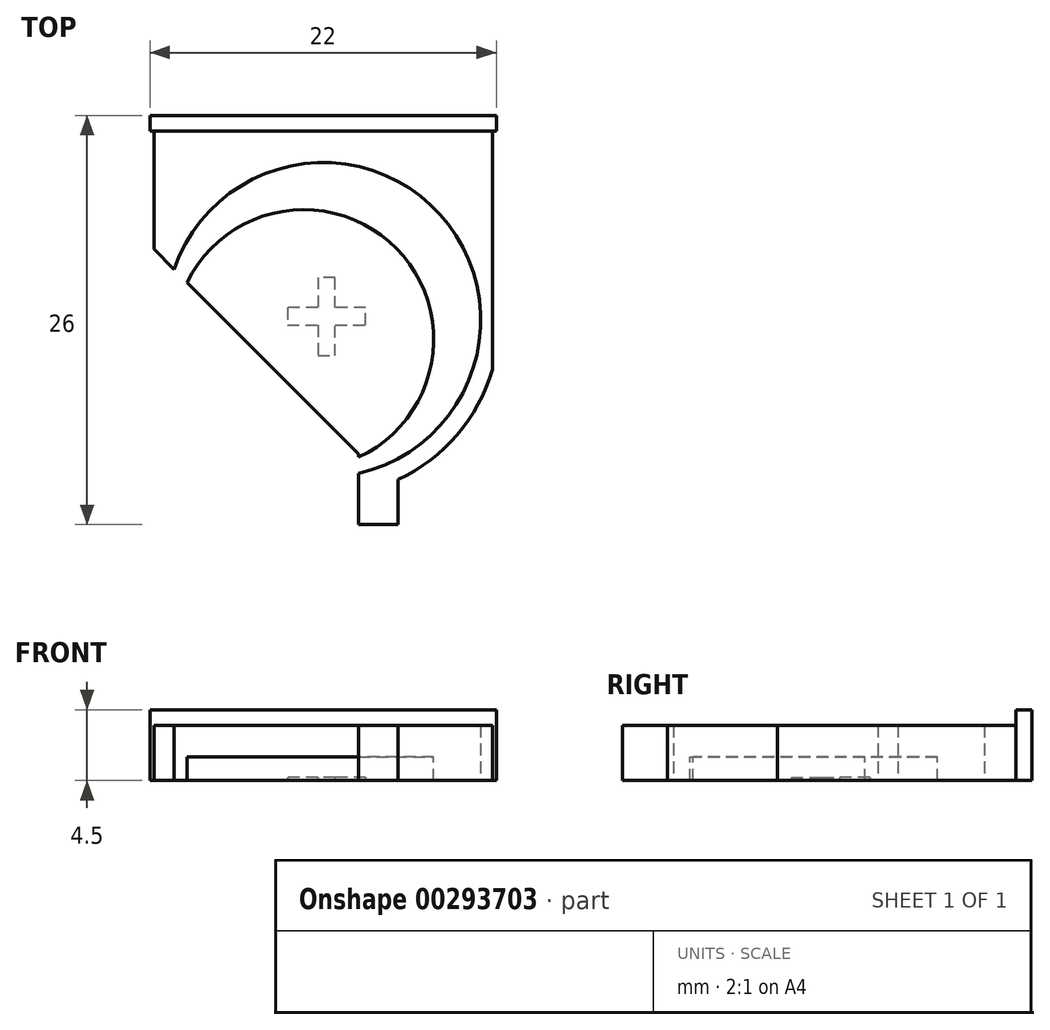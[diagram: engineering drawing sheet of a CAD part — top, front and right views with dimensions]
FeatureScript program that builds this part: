
annotation { "Feature Type Name" : "Feature", "Feature Type Description" : "" }
export const myFeature = defineFeature(function(context is Context, id is Id, definition is map)
    precondition{}
    {
        {
            var Q0;
            Q0=qCreatedBy(makeId("Top.planeOp"),FACE);
            var sketch = newSketch(context, id + "F0", { "sketchPlane" : qUnion([Q0])});
            skLineSegment(sketch, "E0", {"start": v(0, 13) * mm, "end": v(-11, 13) * mm});
            skLineSegment(sketch, "E1", {"start": v(0, 13) * mm, "end": v(11, 13) * mm});
            skLineSegment(sketch, "E2", {"start": v(11, 13) * mm, "end": v(11, 12) * mm});
            skLineSegment(sketch, "E3", {"start": v(-11, 13) * mm, "end": v(-11, 12) * mm});
            skLineSegment(sketch, "E4", {"start": v(-11, 12) * mm, "end": v(11, 12) * mm});
            skPoint(sketch, "E5", {"position": v(-10.75, 12) * mm});
            skPoint(sketch, "E6", {"position": v(10.75, 12) * mm});
            skPoint(sketch, "E7", {"position": v(0, 12) * mm});
            skLineSegment(sketch, "E8", {"start": v(-10.75, 12) * mm, "end": v(-10.75, 9.5) * mm});
            skLineSegment(sketch, "E9", {"start": v(10.75, 12) * mm, "end": v(10.75, 9.5) * mm});
            skLineSegment(sketch, "E10", {"start": v(-10.75, 9.5) * mm, "end": v(10.75, 9.5) * mm});
            skLineSegment(sketch, "E11", {"start": v(-10.75, 9.5) * mm, "end": v(-10.75, 4.5) * mm});
            skLineSegment(sketch, "E12", {"start": v(10.75, 9.5) * mm, "end": v(10.75, -3.14) * mm});
            skArc(sketch, "E13", {"start": v(10.75, -3.14) * mm, "mid": v(8.5, -7.29) * mm, "end": v(4.75, -10.14) * mm});
            skLineSegment(sketch, "E14", {"start": v(4.75, -10.14) * mm, "end": v(4.75, -13) * mm});
            skLineSegment(sketch, "E15", {"start": v(4.75, -13) * mm, "end": v(2.25, -13) * mm});
            skLineSegment(sketch, "E16", {"start": v(2.25, -13) * mm, "end": v(2.25, -8.5) * mm});
            skLineSegment(sketch, "E17", {"start": v(-10.75, 4.5) * mm, "end": v(2.25, -8.5) * mm});
            skLineSegment(sketch, "E18", {"start": v(-10.75, 4.5) * mm, "end": v(10.75, 4.5) * mm, "construction": true});
            skArc(sketch, "E19", {"start": v(-9.47, 3.22) * mm, "mid": v(7.42, 6.7) * mm, "end": v(2.25, -9.74) * mm});
            skCircle(sketch, "E20", {"center": v(-1.24, -1.24) * mm, "radius": 8.25 * mm});
            skArc(sketch, "E21", {"start": v(-9.47, 3.22) * mm, "mid": v(-7.42, -6.7) * mm, "end": v(2.25, -9.74) * mm, "construction": true});
            skLineSegment(sketch, "E22", {"start": v(4.6, 4.6) * mm, "end": v(-7.07, -7.07) * mm});
            skSolve(sketch);
        }
        {
            var Q0;
            Q0=makeQuery(id+"F0.imprint","IMPRINT",FACE,{"disambiguationData":[TD([[makeQuery(id+"F0.imprint","IMPRINT",EDGE,{"derivedFrom":sQuery(id+"F0.wireOp",EDGE,"E0")}),1.0]])]});
            extrude(context, id + "F1", {"entities" : qUnion([Q0]), "depth" : 2.5 * mm, "hasSecondDirection" : true, "secondDirectionOppositeDirection" : true, "secondDirectionDepth" : 2 * mm});
        }
        {
            var Q0;
            {var subQ1=sQuery(id+"F0.wireOp",EDGE,"E8");Q0=makeQuery(id+"F0.imprint","IMPRINT",FACE,{"disambiguationData":[TD([[makeQuery(id+"F0.imprint","IMPRINT",EDGE,{"derivedFrom":subQ1}),1.0]])]});}
            var Q1;
            {var subQ0=sQuery(id+"F0.wireOp",EDGE,"E12");Q1=makeQuery(id+"F0.imprint","IMPRINT",FACE,{"disambiguationData":[TD([[makeQuery(id+"F0.imprint","IMPRINT",EDGE,{"derivedFrom":subQ0}),-1.0]])]});}
            var Q2;
            {var subQ0=sQuery(id+"F0.wireOp",EDGE,"E11");Q2=makeQuery(id+"F0.imprint","IMPRINT",FACE,{"disambiguationData":[TD([[makeQuery(id+"F0.imprint","IMPRINT",EDGE,{"derivedFrom":subQ0}),1.0]])]});}
            var Q3;
            {var subQ0=sQuery(id+"F0.wireOp",EDGE,"E19");var subQ3=sQuery(id+"F0.wireOp",EDGE,"E10");var subQ4=makeQuery(id+"F0.imprint","INTERSECT",VERTEX,{"disambiguationData":[OD(0.0)],"derivedFrom":[subQ3,subQ0]});Q3=makeQuery(id+"F0.imprint","IMPRINT",FACE,{"disambiguationData":[TD([[makeQuery(id+"F0.imprint","IMPRINT",EDGE,{"disambiguationData":[TD([[subQ4,-1.0]])],"derivedFrom":subQ3}),-1.0]])]});}
            var Q4;
            {var subQ0=sQuery(id+"F0.wireOp",EDGE,"E19");var subQ1=sQuery(id+"F0.wireOp",EDGE,"E10");var subQ2=makeQuery(id+"F0.imprint","INTERSECT",VERTEX,{"disambiguationData":[OD(0.0)],"derivedFrom":[subQ1,subQ0]});Q4=makeQuery(id+"F0.imprint","IMPRINT",FACE,{"disambiguationData":[TD([[makeQuery(id+"F0.imprint","IMPRINT",EDGE,{"disambiguationData":[TD([[subQ2,-1.0]])],"derivedFrom":subQ1}),1.0]])]});}
            extrude(context, id + "F2", {"entities" : qUnion([Q0, Q1, Q2, Q3, Q4]), "operationType" : NewBodyOperationType.ADD, "depth" : 1.5 * mm, "hasSecondDirection" : true, "secondDirectionOppositeDirection" : true, "secondDirectionDepth" : 2 * mm});
        }
        {
            var Q0;
            {var subQ0=sQuery(id+"F0.wireOp",EDGE,"E20");var subQ1=sQuery(id+"F0.wireOp",EDGE,"E17");var subQ2=makeQuery(id+"F0.imprint","INTERSECT",VERTEX,{"derivedFrom":[subQ1,subQ0]});Q0=makeQuery(id+"F0.imprint","IMPRINT",FACE,{"disambiguationData":[TD([[makeQuery(id+"F0.imprint","IMPRINT",EDGE,{"disambiguationData":[TD([[subQ2,-1.0]])],"derivedFrom":subQ1}),1.0]])]});}
            var Q1;
            {var subQ0=sQuery(id+"F0.wireOp",EDGE,"E17");var subQ1=sQuery(id+"F0.wireOp",EDGE,"E16");var subQ2=makeQuery(id+"F0.imprint","INTERSECT",VERTEX,{"derivedFrom":[subQ1,subQ0]});Q1=makeQuery(id+"F0.imprint","IMPRINT",FACE,{"disambiguationData":[TD([[makeQuery(id+"F0.imprint","IMPRINT",EDGE,{"disambiguationData":[TD([[subQ2,1.0]])],"derivedFrom":subQ1}),-1.0]])]});}
            var Q2;
            Q2=sQuery(id+"F0.wireOp",EDGE,"E20");
            extrude(context, id + "F3", {"entities" : qUnion([Q0, Q1]), "operationType" : NewBodyOperationType.ADD, "surfaceEntities" : qUnion([Q2]), "oppositeDirection" : true, "depth" : 2 * mm});
        }
        {
            var Q0;
            {var subQ0=sQuery(id+"F0.wireOp",EDGE,"E20");var subQ1=sQuery(id+"F0.wireOp",EDGE,"E17");var subQ2=makeQuery(id+"F0.imprint","INTERSECT",VERTEX,{"derivedFrom":[subQ1,subQ0]});Q0=makeQuery(id+"F0.imprint","IMPRINT",FACE,{"disambiguationData":[TD([[makeQuery(id+"F0.imprint","IMPRINT",EDGE,{"disambiguationData":[TD([[subQ2,-1.0]])],"derivedFrom":subQ1}),1.0]])]});}
            var Q1;
            {var subQ0=sQuery(id+"F0.wireOp",EDGE,"E17");var subQ1=sQuery(id+"F0.wireOp",EDGE,"E16");var subQ2=makeQuery(id+"F0.imprint","INTERSECT",VERTEX,{"derivedFrom":[subQ1,subQ0]});Q1=makeQuery(id+"F0.imprint","IMPRINT",FACE,{"disambiguationData":[TD([[makeQuery(id+"F0.imprint","IMPRINT",EDGE,{"disambiguationData":[TD([[subQ2,1.0]])],"derivedFrom":subQ1}),-1.0]])]});}
            extrude(context, id + "F4", {"entities" : qUnion([Q0, Q1]), "operationType" : NewBodyOperationType.REMOVE, "oppositeDirection" : true, "depth" : 0.5 * mm});
        }
        {
            var Q0;
            {var subQ0=sQuery(id+"F0.wireOp",EDGE,"E20");var subQ1=sQuery(id+"F0.wireOp",EDGE,"E17");var subQ2=sQuery(id+"F0.wireOp",EDGE,"E16");var subQ3=sQuery(id+"F0.wireOp",EDGE,"E4");Q0=makeQuery(id+"F3.boolean.opBoolean","MERGE",FACE,{"derivedFrom":[makeQuery(id+"F2.boolean.opBoolean","MERGE",FACE,{"derivedFrom":[makeQuery(id+"F1.opExtrude","CAP_FACE",FACE,{"disambiguationData":[OSD([sQuery(id+"F0.wireOp",EDGE,"E0"),sQuery(id+"F0.wireOp",EDGE,"E1"),sQuery(id+"F0.wireOp",EDGE,"E2"),sQuery(id+"F0.wireOp",EDGE,"E3"),subQ3])],"isStart":true}),makeQuery(id+"F2.opExtrude","CAP_FACE",FACE,{"disambiguationData":[OSD([subQ3,sQuery(id+"F0.wireOp",EDGE,"E8"),sQuery(id+"F0.wireOp",EDGE,"E9"),sQuery(id+"F0.wireOp",EDGE,"E11"),sQuery(id+"F0.wireOp",EDGE,"E12"),sQuery(id+"F0.wireOp",EDGE,"E13"),sQuery(id+"F0.wireOp",EDGE,"E14"),sQuery(id+"F0.wireOp",EDGE,"E15"),subQ2,subQ1,subQ0])],"isStart":true})]}),makeQuery(id+"F3.opExtrude","CAP_FACE",FACE,{"disambiguationData":[OSD([subQ2,subQ1,subQ0])],"isStart":false})]});}
            var sketch = newSketch(context, id + "F5", { "sketchPlane" : qUnion([Q0])});
            skText(sketch, "E23", { "text": "+", "fontName": "OpenSans-Bold.ttf"});
            const initialGuessF5  = {"E23": [-0.00272, -0.00385, 1, 0, 0.00739]};
            skSetInitialGuess(sketch, initialGuessF5);
            skSolve(sketch);
        }
        {
            var Q0;
            Q0=makeQuery(id+"F5.imprint","IMPRINT",FACE,{"disambiguationData":[TD([[makeQuery(id+"F5.imprint","IMPRINT",EDGE,{"derivedFrom":sQuery(id+"F5.wireOp",EDGE,"E23.sketch_text.stroke-0")}),-1.0]])]});
            extrude(context, id + "F6", {"entities" : qUnion([Q0]), "operationType" : NewBodyOperationType.REMOVE, "oppositeDirection" : true, "depth" : 0.2 * mm});
        }
    });
